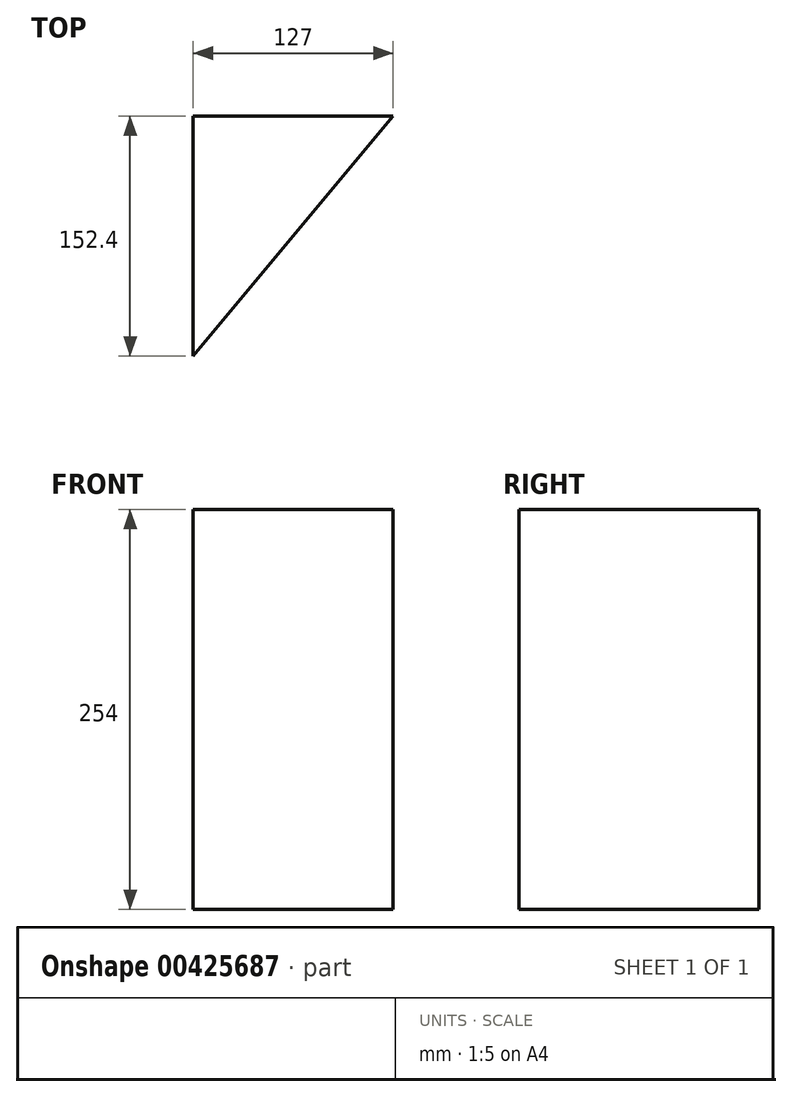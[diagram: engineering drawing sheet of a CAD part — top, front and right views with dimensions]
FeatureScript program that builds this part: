
annotation { "Feature Type Name" : "Feature", "Feature Type Description" : "" }
export const myFeature = defineFeature(function(context is Context, id is Id, definition is map)
    precondition{}
    {
        {
            var Q0;
            Q0=qCreatedBy(makeId("Top.planeOp"),FACE);
            var sketch = newSketch(context, id + "F0", { "sketchPlane" : qUnion([Q0])});
            skLineSegment(sketch, "E0", {"start": v(-60.62, 152.4) * mm, "end": v(-60.62, 0) * mm});
            skLineSegment(sketch, "E1", {"start": v(-60.62, 152.4) * mm, "end": v(66.38, 152.4) * mm});
            skLineSegment(sketch, "E2", {"start": v(-60.62, 0) * mm, "end": v(66.38, 152.4) * mm});
            skSolve(sketch);
        }
        {
            var Q0;
            Q0 = qSketchRegion(id + "F0", true);
            extrude(context, id + "F1", {"entities" : qUnion([Q0]), "depth" : 254 * mm});
        }
    });
